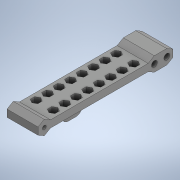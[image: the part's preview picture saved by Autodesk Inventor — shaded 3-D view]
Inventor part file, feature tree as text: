
AUTODESK INVENTOR PART (.ipt)
format: ipt  version: 2020 (Build 240168000, 168)  size: 513,024 bytes
history: native  units: in
note: dims shown in document units (in); Inventor stores cm internally (conversion verified against a paired STEP export)
features: sketch x7, extrude x6, projected_geometry x4, plane x2, mirror x1, fillet x1
ambient origin geometry x8: Origin, YZ Plane, XZ Plane, XY Plane, X Axis, Y Axis, Z Axis, Center Point
bodies: Solid1 (feature_tree)
feature tree (21):
  extrude  "Extrusion1"  Depth=3.4256in
  plane  "Work Plane1"
  extrude  "Extrusion2"  Depth=0.7874in
  sketch  "Sketch4"  dims[d4=0.0in d5=0.0827in]
  extrude  "Extrusion4"  Depth=0.0827in
  plane  "Work Plane2"
  extrude  "Extrusion6"  Depth=3.1106in
  mirror  "Mirror2"
  extrude  "Extrusion7"  Depth=0.315in
  extrude  "Extrusion8"  Depth=0.2362in
  fillet  "Fillet1"  [1 undecoded]
  sketch  "Sketch1"  dims[d0=0.1818in d1=3.4256in]
  sketch  "Sketch2"  dims[d2=0.0984in d3=0.7874in]
  sketch  "Sketch5"  dims[d6=0.7874in d7=0.0in d28=3.1106in]
  sketch  "Sketch7"  dims[d29=0.315in d31=0.315in]
  projected_geometry  "Projected Loop7"
  projected_geometry  "Projected Loop8"
  sketch  "Sketch8"  dims[d33=0.1476in d34=0.2362in d35=0.0in]
  projected_geometry  "Projected Loop9"
  sketch  "Sketch10"  dims[d38=0.315in d39=0.2756in d40=-0.3092in d41=0.0787in d42=0.0787in d43=0.0787in d44=3.1496in d46=0.2913in d47=0.3937in d49=0.3937in d51=3.1496in d53=0.2913in d54=0.3937in d56=0.3937in d58=0.0in d59=0.0in d60=1.0994in d61=0.1378in d63=1.1811in d64=0.1575in d65=0.0in d66=0.126in d67=0.1575in]
  projected_geometry  "Projected Loop10"
note: 1 required parameter value undecoded (feature->parameter linkage not recoverable at this tier; creation-order binding heuristic only, values carry confidence <= 0.55)
